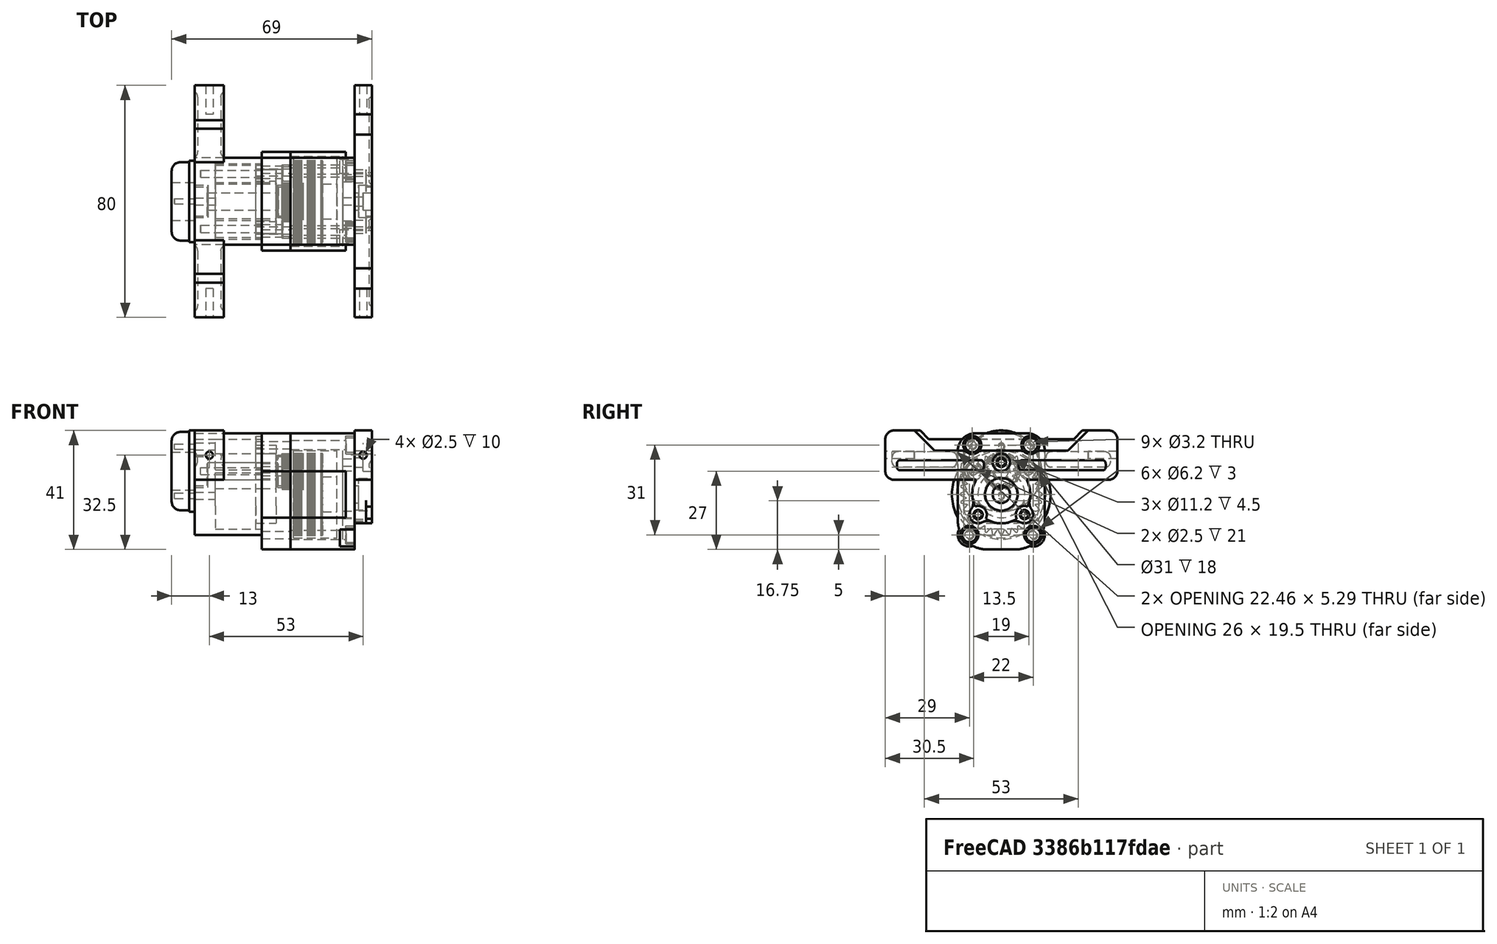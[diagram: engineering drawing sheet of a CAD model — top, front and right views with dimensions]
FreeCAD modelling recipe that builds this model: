
FCSTD DOCUMENT  (FreeCAD 0.14R3702 (Git))
Label: transfercase_box_02
License: CC-BY 3.0
LicenseURL: http://creativecommons.org/licenses/by/3.0/
objects: Part::Cylinder×106, Part::MultiFuse×53, Part::Cut×45, Part::Fillet×36, Part::Box×27, Part::Chamfer×3, Part::Feature×2
note: 272 computed .brp shape members not serialized (recipe doc carries the construction recipe); baked Part::Feature solids carry a one-line shape summary decoded from their .brp

FEATURE [Part::Box] Box
  Height = 40
  Length = 32
  Placement = pos=(23,0,0) rot=(0,0,1;0rad)
  Width = 30
FEATURE [Part::Box] Box001
  Height = 35
  Length = 23
  Placement = pos=(0,0,5) rot=(0,0,1;0rad)
  Width = 30
FEATURE [Part::Cylinder] Cylinder002
  Angle = 360
  Height = 6
  Placement = pos=(55,15,19) rot=(0,1,0;1.5708rad)
  Radius = 10
FEATURE [Part::Feature] difference002
  Placement = pos=(34,15,22) rot=(0,1,0;1.5708rad)
  shape: bbox 15 x 30 x 30 mm, 387 faces (baked)
FEATURE [Part::Cylinder] Cylinder003
  Angle = 360
  Height = 19
  Placement = pos=(33,15,19) rot=(0,1,0;1.5708rad)
  Radius = 17
FEATURE [Part::Feature] difference003
  Placement = pos=(29,16,29.5) rot=(0,1,0;1.5708rad)
  shape: bbox 15 x 12.44 x 12.35 mm, 184 faces (baked)
FEATURE [Part::Cylinder] Cylinder004
  Angle = 360
  Height = 4
  Placement = pos=(29,16,29.5) rot=(0,1,0;1.5708rad)
  Radius = 6.3
FEATURE [Part::Cut] Cut001
  Base = -> difference003
  Tool = -> Cylinder004
FEATURE [Part::Cylinder] Cylinder005
  Angle = 360
  Height = 1
  Placement = pos=(33,16,29.5) rot=(0,1,0;1.5708rad)
  Radius = 6.3
FEATURE [Part::MultiFuse] Fusion002
  Shapes = -> [Cylinder005,Cut001]
FEATURE [Part::Cylinder] Cylinder006
  Angle = 360
  Height = 5
  Placement = pos=(44,15,22) rot=(0,1,0;1.5708rad)
  Radius = 15
FEATURE [Part::MultiFuse] Fusion003
  Shapes = -> [difference002,Cylinder006]
FEATURE [Part::Cylinder] Cylinder007
  Angle = 360
  Height = 11
  Placement = pos=(33,16,29.5) rot=(0,1,0;1.5708rad)
  Radius = 2.5
FEATURE [Part::Box] Box002
  Height = 10
  Length = 10
  Placement = pos=(39,12,29.5) rot=(0,0,1;0rad)
  Width = 10
FEATURE [Part::Cut] Cut002
  Base = -> Cylinder007
  Tool = -> Box002
FEATURE [Part::Cut] Cut003  label="inner-gear_"
  Base = -> Fusion002
  Placement = pos=(-5,-1,-2.5) rot=(0,0,1;0rad)
  Tool = -> Cut002
FEATURE [Part::Cylinder] Cylinder009
  Angle = 360
  Height = 5
  Placement = pos=(44,15,22) rot=(0,1,0;1.5708rad)
  Radius = 6
FEATURE [Part::Cut] Cut004  label="outer-gear"
  Base = -> Fusion003
  Placement = pos=(0,0,-3) rot=(0,0,1;0rad)
  Tool = -> Cylinder009
FEATURE [Part::Fillet] Fillet002
  Base = -> Box001
  Edges = 2 edges r=10: [Edge9,Edge11]
FEATURE [Part::Fillet] Fillet003
  Base = -> Box
  Edges = 2 edges r=10: [Edge9,Edge11]
FEATURE [Part::Fillet] Fillet004
  Base = -> Fillet002
  Edges = 2 edges r=6: [Edge9,Edge12]
FEATURE [Part::Fillet] Fillet005
  Base = -> Fillet003
  Edges = 2 edges r=6: [Edge9,Edge12]
FEATURE [Part::MultiFuse] Fusion004
  Shapes = -> [Fillet005,Fillet004]
FEATURE [Part::Cylinder] Cylinder011
  Angle = 360
  Height = 2
  Placement = pos=(-2,15,27) rot=(0,1,0;1.5708rad)
  Radius = 14
FEATURE [Part::MultiFuse] Fusion006
  Shapes = -> [Fusion004,Cylinder003]
FEATURE [Part::Box] Box003  label="Cube"
  Height = 17
  Length = 10
  Placement = pos=(0,-25,24) rot=(0,0,1;0rad)
  Width = 80
FEATURE [Part::Fillet] Fillet006
  Base = -> Box003
  Edges = 4 edges r=3: [Edge9,Edge10,Edge11,Edge12]
FEATURE [Part::Box] Box004  label="Cube001"
  Height = 3
  Length = 10
  Placement = pos=(0,-10,38) rot=(0,0,1;0rad)
  Width = 50
FEATURE [Part::Cut] Cut
  Base = -> Fillet006
  Tool = -> Box004
FEATURE [Part::Chamfer] Chamfer
  Base = -> Cut
  Edges = 2 edges r=2.99: [Edge18,Edge25]
FEATURE [Part::Box] Box005
  Height = 35
  Length = 23
  Placement = pos=(0,0,5) rot=(0,0,1;0rad)
  Width = 30
FEATURE [Part::Cylinder] Cylinder
  Angle = 360
  Height = 17
  Placement = pos=(33,15,18) rot=(0,1,0;1.5708rad)
  Radius = 17
FEATURE [Part::Box] Box006
  Height = 40
  Length = 32
  Placement = pos=(23,0,0) rot=(0,0,1;0rad)
  Width = 30
FEATURE [Part::Fillet] Fillet
  Base = -> Box006
  Edges = 2 edges r=10: [Edge9,Edge11]
FEATURE [Part::Fillet] Fillet007
  Base = -> Fillet
  Edges = 2 edges r=6: [Edge9,Edge12]
FEATURE [Part::Fillet] Fillet008
  Base = -> Box005
  Edges = 2 edges r=10: [Edge9,Edge11]
FEATURE [Part::Fillet] Fillet009
  Base = -> Fillet008
  Edges = 2 edges r=6: [Edge9,Edge12]
FEATURE [Part::MultiFuse] Fusion007
  Shapes = -> [Fillet007,Fillet009]
FEATURE [Part::MultiFuse] Fusion
  Shapes = -> [Fusion007,Cylinder]
FEATURE [Part::Box] Box007
  Height = 40
  Length = 33
  Width = 30
FEATURE [Part::Box] Box008
  Height = 40
  Length = 22
  Placement = pos=(33,-3,0) rot=(0,0,1;0rad)
  Width = 36
FEATURE [Part::Cut] Cut005
  Base = -> Fusion006
  Tool = -> Box007
FEATURE [Part::Cut] Cut006
  Base = -> Fusion
  Tool = -> Box008
FEATURE [Part::Cylinder] Cylinder012
  Angle = 360
  Height = 18
  Placement = pos=(33,15,19) rot=(0,1,0;1.5708rad)
  Radius = 15.5
FEATURE [Part::Cylinder] Cylinder013
  Angle = 360
  Height = 25
  Placement = pos=(30,0,19) rot=(0,1,0;1.5708rad)
  Radius = 1.6
FEATURE [Part::Cylinder] Cylinder014
  Angle = 360
  Height = 4
  Placement = pos=(51,0,19) rot=(0,1,0;1.5708rad)
  Radius = 3.1
FEATURE [Part::MultiFuse] Fusion008
  Placement = pos=(0,4,-14) rot=(0,0,1;0rad)
  Shapes = -> [Cylinder014,Cylinder013]
FEATURE [Part::Cylinder] Cylinder015
  Angle = 360
  Height = 25
  Placement = pos=(30,0,19) rot=(0,1,0;1.5708rad)
  Radius = 1.6
FEATURE [Part::Cylinder] Cylinder016
  Angle = 360
  Height = 4
  Placement = pos=(51,0,19) rot=(0,1,0;1.5708rad)
  Radius = 3.1
FEATURE [Part::MultiFuse] Fusion009
  Placement = pos=(0,5,17) rot=(0,0,1;0rad)
  Shapes = -> [Cylinder016,Cylinder015]
FEATURE [Part::Cylinder] Cylinder017
  Angle = 360
  Height = 25
  Placement = pos=(30,0,19) rot=(0,1,0;1.5708rad)
  Radius = 1.6
FEATURE [Part::Cylinder] Cylinder018
  Angle = 360
  Height = 4
  Placement = pos=(51,0,19) rot=(0,1,0;1.5708rad)
  Radius = 3.1
FEATURE [Part::MultiFuse] Fusion010
  Placement = pos=(0,25,17) rot=(0,0,1;0rad)
  Shapes = -> [Cylinder018,Cylinder017]
FEATURE [Part::Cylinder] Cylinder019
  Angle = 360
  Height = 25
  Placement = pos=(30,0,19) rot=(0,1,0;1.5708rad)
  Radius = 1.6
FEATURE [Part::Cylinder] Cylinder020
  Angle = 360
  Height = 4
  Placement = pos=(51,0,19) rot=(0,1,0;1.5708rad)
  Radius = 3.1
FEATURE [Part::MultiFuse] Fusion011
  Placement = pos=(0,26,-14) rot=(0,0,1;0rad)
  Shapes = -> [Cylinder020,Cylinder019]
FEATURE [Part::Cylinder] Cylinder021
  Angle = 360
  Height = 5
  Placement = pos=(50,4,5) rot=(0,1,0;1.5708rad)
  Radius = 4
FEATURE [Part::Cylinder] Cylinder022
  Angle = 360
  Height = 5
  Placement = pos=(50,26,5) rot=(0,1,0;1.5708rad)
  Radius = 4
FEATURE [Part::MultiFuse] Fusion013
  Placement = pos=(1,0,0) rot=(0,0,1;0rad)
  Shapes = -> [Fusion008,Fusion010,Fusion011,Fusion009]
FEATURE [Part::MultiFuse] Fusion014
  Shapes = -> [Cut005,Cylinder022,Cylinder021]
FEATURE [Part::Cut] Cut007
  Base = -> Fusion014
  Tool = -> Cylinder012
FEATURE [Part::Cut] Cut008
  Base = -> Cut007
  Tool = -> Fusion013
FEATURE [Part::Cylinder] Cylinder023
  Angle = 360
  Height = 10
  Placement = pos=(23,15,19) rot=(0,1,0;1.5708rad)
  Radius = 17
FEATURE [Part::MultiFuse] Fusion015
  Shapes = -> [Cut006,Cylinder023]
FEATURE [Part::Cylinder] Cylinder024
  Angle = 360
  Height = 15
  Placement = pos=(30,5,36) rot=(0,1,0;1.5708rad)
  Radius = 1.25
FEATURE [Part::Cylinder] Cylinder025
  Angle = 360
  Height = 15
  Placement = pos=(30,25,36) rot=(0,1,0;1.5708rad)
  Radius = 1.25
FEATURE [Part::Cylinder] Cylinder026
  Angle = 360
  Height = 15
  Placement = pos=(30,26,5) rot=(0,1,0;1.5708rad)
  Radius = 1.25
FEATURE [Part::Cylinder] Cylinder027
  Angle = 360
  Height = 15
  Placement = pos=(30,4,5) rot=(0,1,0;1.5708rad)
  Radius = 1.25
FEATURE [Part::MultiFuse] Fusion016
  Placement = pos=(-12,0,0) rot=(0,0,1;0rad)
  Shapes = -> [Cylinder024,Cylinder027,Cylinder026,Cylinder025]
FEATURE [Part::Cut] Cut009
  Base = -> Fusion015
  Tool = -> Fusion016
FEATURE [Part::Cylinder] Cylinder029
  Angle = 360
  Height = 4.5
  Placement = pos=(28.5,15,27) rot=(0,1,0;1.5708rad)
  Radius = 5.6
FEATURE [Part::Cylinder] Cylinder030
  Angle = 360
  Height = 4.5
  Placement = pos=(0,15,27) rot=(0,1,0;1.5708rad)
  Radius = 5.6
FEATURE [Part::MultiFuse] Fusion017
  Shapes = -> [Chamfer,Cut009]
FEATURE [Part::Cylinder] Cylinder031
  Angle = 360
  Height = 33
  Placement = pos=(0,15,27) rot=(0,1,0;1.5708rad)
  Radius = 3
FEATURE [Part::MultiFuse] Fusion018
  Shapes = -> [Cylinder031,Cylinder030,Cylinder029]
FEATURE [Part::Cut] Cut010
  Base = -> Fusion017
  Tool = -> Fusion018
FEATURE [Part::Cylinder] Cylinder032
  Angle = 360
  Height = 5
  Placement = pos=(51,15,19) rot=(0,1,0;1.5708rad)
  Radius = 8.1
FEATURE [Part::Cut] Cut011
  Base = -> Cut008
  Tool = -> Cylinder032
FEATURE [Part::Cylinder] Cylinder033
  Angle = 360
  Height = 4
  Placement = pos=(57,15,19) rot=(0,1,0;1.5708rad)
  Radius = 5.6
FEATURE [Part::Cylinder] Cylinder034
  Angle = 360
  Height = 5
  Placement = pos=(55,15,19) rot=(0,1,0;1.5708rad)
  Radius = 3
FEATURE [Part::MultiFuse] Fusion019
  Shapes = -> [Cylinder033,Cylinder034]
FEATURE [Part::Cut] Cut012
  Base = -> Cylinder002
  Tool = -> Fusion019
FEATURE [Part::Cylinder] Cylinder035
  Angle = 360
  Height = 6
  Placement = pos=(55,23,12) rot=(0,1,0;1.5708rad)
  Radius = 3
FEATURE [Part::Box] Box009  label="Cube002"
  Height = 10
  Length = 6
  Placement = pos=(55,-25,24) rot=(0,0,1;0rad)
  Width = 80
FEATURE [Part::Cylinder] Cylinder036
  Angle = 360
  Height = 23
  Placement = pos=(-3,0,31) rot=(1,0,0;1.5708rad)
  Radius = 4
FEATURE [Part::Fillet] Fillet010
  Base = -> Cylinder036
  Edges = 2 edges r=2: [Edge1,Edge3]
FEATURE [Part::Cylinder] Cylinder037
  Angle = 360
  Height = 23
  Placement = pos=(-3,0,31) rot=(1,0,0;1.5708rad)
  Radius = 4
FEATURE [Part::Fillet] Fillet011
  Base = -> Cylinder037
  Edges = 2 edges r=2: [Edge1,Edge3]
  Placement = pos=(0,53,0) rot=(0,0,1;0rad)
FEATURE [Part::Cylinder] Cylinder038
  Angle = 360
  Height = 23
  Placement = pos=(-3,0,31) rot=(1,0,0;1.5708rad)
  Radius = 4
FEATURE [Part::Cylinder] Cylinder039
  Angle = 360
  Height = 23
  Placement = pos=(-3,0,31) rot=(1,0,0;1.5708rad)
  Radius = 4
FEATURE [Part::Fillet] Fillet012
  Base = -> Cylinder039
  Edges = 2 edges r=2: [Edge1,Edge3]
  Placement = pos=(16,0,0) rot=(0,0,1;0rad)
FEATURE [Part::Fillet] Fillet013
  Base = -> Cylinder038
  Edges = 2 edges r=2: [Edge1,Edge3]
  Placement = pos=(16,53,0) rot=(0,0,1;0rad)
FEATURE [Part::MultiFuse] Fusion020
  Shapes = -> [Fillet010,Fillet012,Fillet011,Fillet013]
FEATURE [Part::Cut] Cut013
  Base = -> Cut010
  Tool = -> Fusion020
FEATURE [Part::Cylinder] Cylinder040
  Angle = 360
  Height = 6
  Placement = pos=(55,7,12) rot=(0,1,0;1.5708rad)
  Radius = 3
FEATURE [Part::MultiFuse] Fusion021
  Shapes = -> [Cut012,Cylinder035,Cylinder040]
FEATURE [Part::Cylinder] Cylinder041
  Angle = 360
  Height = 3
  Placement = pos=(58,23,12) rot=(0,1,0;1.5708rad)
  Radius = 3
FEATURE [Part::Cylinder] Cylinder042
  Angle = 360
  Height = 3
  Placement = pos=(58,7,12) rot=(0,1,0;1.5708rad)
  Radius = 3
FEATURE [Part::Cylinder] Cylinder043
  Angle = 360
  Height = 10
  Placement = pos=(51,7,12) rot=(0,1,0;1.5708rad)
  Radius = 1.6
FEATURE [Part::Cylinder] Cylinder044
  Angle = 360
  Height = 10
  Placement = pos=(51,23,12) rot=(0,1,0;1.5708rad)
  Radius = 1.6
FEATURE [Part::MultiFuse] Fusion022
  Placement = pos=(1,0,0) rot=(0,0,1;0rad)
  Shapes = -> [Cylinder041,Cylinder042,Cylinder043,Cylinder044]
FEATURE [Part::Cut] Cut014
  Base = -> Fusion021
  Tool = -> Fusion022
FEATURE [Part::Cylinder] Cylinder045
  Angle = 360
  Height = 10
  Placement = pos=(47,7,12) rot=(0,1,0;1.5708rad)
  Radius = 1.25
FEATURE [Part::Cylinder] Cylinder046
  Angle = 360
  Height = 10
  Placement = pos=(46,23,12) rot=(0,1,0;1.5708rad)
  Radius = 1.25
FEATURE [Part::MultiFuse] Fusion023
  Shapes = -> [Cylinder046,Cylinder045]
FEATURE [Part::Cut] Cut015
  Base = -> Cut011
  Tool = -> Fusion023
FEATURE [Part::Box] Box010  label="Cube003"
  Height = 17
  Length = 6
  Placement = pos=(55,-25,24) rot=(0,0,1;0rad)
  Width = 10
FEATURE [Part::Box] Box011  label="Cube004"
  Height = 17
  Length = 6
  Placement = pos=(55,45,24) rot=(0,0,1;0rad)
  Width = 10
FEATURE [Part::Cylinder] Cylinder047
  Angle = 360
  Height = 3
  Placement = pos=(58,22,12) rot=(0,1,0;1.5708rad)
  Radius = 3
FEATURE [Part::Cylinder] Cylinder048
  Angle = 360
  Height = 10
  Placement = pos=(48,22,12) rot=(0,1,0;1.5708rad)
  Radius = 1.6
FEATURE [Part::MultiFuse] Fusion024
  Placement = pos=(0,-7,18) rot=(0,0,1;0rad)
  Shapes = -> [Cylinder048,Cylinder047]
FEATURE [Part::Cylinder] Cylinder049
  Angle = 360
  Height = 6
  Placement = pos=(55,15,19) rot=(0,1,0;1.5708rad)
  Radius = 5.6
FEATURE [Part::Cut] Cut016
  Base = -> Box009
  Tool = -> Cylinder049
FEATURE [Part::MultiFuse] Fusion025
  Shapes = -> [Box010,Box011,Cut016,Cut014]
FEATURE [Part::Cut] Cut017
  Base = -> Fusion025
  Tool = -> Fusion024
FEATURE [Part::Cylinder] Cylinder050
  Angle = 360
  Height = 10
  Placement = pos=(48,15,30) rot=(0,1,0;1.5708rad)
  Radius = 1.25
FEATURE [Part::Cut] Cut018  label="rear-part"
  Base = -> Cut015
  Tool = -> Cylinder050
FEATURE [Part::Fillet] Fillet014
  Base = -> Cut017
  Edges = 4 edges r=3: [Edge4,Edge44,Edge50,Edge53]
FEATURE [Part::Chamfer] Chamfer001
  Base = -> Fillet014
  Edges = 2 edges r=6.99: [Edge32,Edge54]
FEATURE [Part::Cylinder] Cylinder051
  Angle = 360
  Height = 10
  Placement = pos=(5,55,32.5) rot=(1,0,0;1.5708rad)
  Radius = 1.25
FEATURE [Part::Cylinder] Cylinder052
  Angle = 360
  Height = 10
  Placement = pos=(58,-15,32.5) rot=(1,0,0;1.5708rad)
  Radius = 1.25
FEATURE [Part::Cylinder] Cylinder053
  Angle = 360
  Height = 10
  Placement = pos=(5,-15,32.5) rot=(1,0,0;1.5708rad)
  Radius = 1.25
FEATURE [Part::Cylinder] Cylinder054
  Angle = 360
  Height = 10
  Placement = pos=(58,55,32.5) rot=(1,0,0;1.5708rad)
  Radius = 1.25
FEATURE [Part::MultiFuse] Fusion026
  Shapes = -> [Cylinder053,Cylinder051]
FEATURE [Part::MultiFuse] Fusion027
  Shapes = -> [Cylinder054,Cylinder052]
FEATURE [Part::Cut] Cut019
  Base = -> Cut013
  Tool = -> Fusion026
FEATURE [Part::Cylinder] Cylinder055
  Angle = 360
  Height = 10
  Placement = pos=(-10,15,27) rot=(0,1,0;1.5708rad)
  Radius = 6.5
FEATURE [Part::Cylinder] Cylinder056
  Angle = 360
  Height = 30
  Placement = pos=(62,9,29) rot=(1,0,0;1.5708rad)
  Radius = 2
FEATURE [Part::Fillet] Fillet016
  Base = -> Cylinder056
  Edges = 2 edges r=1: [Edge1,Edge3]
FEATURE [Part::Cylinder] Cylinder057
  Angle = 360
  Height = 30
  Placement = pos=(62,9,29) rot=(1,0,0;1.5708rad)
  Radius = 2
FEATURE [Part::Fillet] Fillet017
  Base = -> Cylinder057
  Edges = 2 edges r=1: [Edge1,Edge3]
  Placement = pos=(0,42,0) rot=(0,0,1;0rad)
FEATURE [Part::MultiFuse] Fusion028
  Shapes = -> [Fillet016,Fillet017]
FEATURE [Part::Cylinder] Cylinder058
  Angle = 360
  Height = 6
  Placement = pos=(-8,15,27) rot=(0,1,0;1.5708rad)
  Radius = 13.5
FEATURE [Part::MultiFuse] Fusion029
  Shapes = -> [Cylinder011,Cylinder058]
FEATURE [Part::Box] Box012  label="Cube005"
  Height = 17
  Length = 10
  Placement = pos=(0,-25,24) rot=(0,0,1;0rad)
  Width = 80
FEATURE [Part::Fillet] Fillet018
  Base = -> Box012
  Edges = 4 edges r=3: [Edge9,Edge10,Edge11,Edge12]
FEATURE [Part::Box] Box013  label="Cube006"
  Height = 3
  Length = 10
  Placement = pos=(0,-10,38) rot=(0,0,1;0rad)
  Width = 50
FEATURE [Part::Cut] Cut027
  Base = -> Fillet018
  Tool = -> Box013
FEATURE [Part::Chamfer] Chamfer002
  Base = -> Cut027
  Edges = 2 edges r=2.99: [Edge18,Edge25]
FEATURE [Part::Box] Box014
  Height = 40
  Length = 32
  Placement = pos=(23,0,0) rot=(0,0,1;0rad)
  Width = 30
FEATURE [Part::Fillet] Fillet020
  Base = -> Box014
  Edges = 2 edges r=10: [Edge9,Edge11]
FEATURE [Part::Fillet] Fillet019
  Base = -> Fillet020
  Edges = 2 edges r=6: [Edge9,Edge12]
FEATURE [Part::Box] Box015
  Height = 35
  Length = 23
  Placement = pos=(0,0,5) rot=(0,0,1;0rad)
  Width = 30
FEATURE [Part::Fillet] Fillet022
  Base = -> Box015
  Edges = 2 edges r=10: [Edge9,Edge11]
FEATURE [Part::Fillet] Fillet021
  Base = -> Fillet022
  Edges = 2 edges r=6: [Edge9,Edge12]
FEATURE [Part::MultiFuse] Fusion034
  Shapes = -> [Fillet019,Fillet021]
FEATURE [Part::Cylinder] Cylinder060
  Angle = 360
  Height = 17
  Placement = pos=(33,15,18) rot=(0,1,0;1.5708rad)
  Radius = 17
FEATURE [Part::MultiFuse] Fusion033
  Shapes = -> [Fusion034,Cylinder060]
FEATURE [Part::Box] Box016
  Height = 40
  Length = 22
  Placement = pos=(33,-3,0) rot=(0,0,1;0rad)
  Width = 36
FEATURE [Part::Cut] Cut029
  Base = -> Fusion033
  Tool = -> Box016
FEATURE [Part::Cylinder] Cylinder061
  Angle = 360
  Height = 10
  Placement = pos=(23,15,19) rot=(0,1,0;1.5708rad)
  Radius = 17
FEATURE [Part::MultiFuse] Fusion032
  Shapes = -> [Cut029,Cylinder061]
FEATURE [Part::Cylinder] Cylinder062
  Angle = 360
  Height = 15
  Placement = pos=(30,5,36) rot=(0,1,0;1.5708rad)
  Radius = 1.25
FEATURE [Part::Cylinder] Cylinder063
  Angle = 360
  Height = 15
  Placement = pos=(30,4,5) rot=(0,1,0;1.5708rad)
  Radius = 1.25
FEATURE [Part::Cylinder] Cylinder064
  Angle = 360
  Height = 15
  Placement = pos=(30,26,5) rot=(0,1,0;1.5708rad)
  Radius = 1.25
FEATURE [Part::Cylinder] Cylinder065
  Angle = 360
  Height = 15
  Placement = pos=(30,25,36) rot=(0,1,0;1.5708rad)
  Radius = 1.25
FEATURE [Part::MultiFuse] Fusion035
  Placement = pos=(-12,0,0) rot=(0,0,1;0rad)
  Shapes = -> [Cylinder062,Cylinder063,Cylinder064,Cylinder065]
FEATURE [Part::Cut] Cut028
  Base = -> Fusion032
  Tool = -> Fusion035
FEATURE [Part::MultiFuse] Fusion031
  Shapes = -> [Chamfer002,Cut028]
FEATURE [Part::Cylinder] Cylinder066
  Angle = 360
  Height = 33
  Placement = pos=(0,15,27) rot=(0,1,0;1.5708rad)
  Radius = 3
FEATURE [Part::Cylinder] Cylinder067
  Angle = 360
  Height = 4.5
  Placement = pos=(0,15,27) rot=(0,1,0;1.5708rad)
  Radius = 5.6
FEATURE [Part::Cylinder] Cylinder068
  Angle = 360
  Height = 4.5
  Placement = pos=(28.5,15,27) rot=(0,1,0;1.5708rad)
  Radius = 5.6
FEATURE [Part::MultiFuse] Fusion036
  Shapes = -> [Cylinder066,Cylinder067,Cylinder068]
FEATURE [Part::Cut] Cut026
  Base = -> Fusion031
  Tool = -> Fusion036
FEATURE [Part::Cylinder] Cylinder069
  Angle = 360
  Height = 23
  Placement = pos=(-3,0,31) rot=(1,0,0;1.5708rad)
  Radius = 4
FEATURE [Part::Fillet] Fillet023
  Base = -> Cylinder069
  Edges = 2 edges r=2: [Edge1,Edge3]
FEATURE [Part::Cylinder] Cylinder070
  Angle = 360
  Height = 23
  Placement = pos=(-3,0,31) rot=(1,0,0;1.5708rad)
  Radius = 4
FEATURE [Part::Fillet] Fillet024
  Base = -> Cylinder070
  Edges = 2 edges r=2: [Edge1,Edge3]
  Placement = pos=(16,0,0) rot=(0,0,1;0rad)
FEATURE [Part::Cylinder] Cylinder071
  Angle = 360
  Height = 23
  Placement = pos=(-3,0,31) rot=(1,0,0;1.5708rad)
  Radius = 4
FEATURE [Part::Fillet] Fillet025
  Base = -> Cylinder071
  Edges = 2 edges r=2: [Edge1,Edge3]
  Placement = pos=(0,53,0) rot=(0,0,1;0rad)
FEATURE [Part::Cylinder] Cylinder072
  Angle = 360
  Height = 23
  Placement = pos=(-3,0,31) rot=(1,0,0;1.5708rad)
  Radius = 4
FEATURE [Part::Fillet] Fillet026
  Base = -> Cylinder072
  Edges = 2 edges r=2: [Edge1,Edge3]
  Placement = pos=(16,53,0) rot=(0,0,1;0rad)
FEATURE [Part::MultiFuse] Fusion037
  Shapes = -> [Fillet023,Fillet024,Fillet025,Fillet026]
FEATURE [Part::Cut] Cut025
  Base = -> Cut026
  Tool = -> Fusion037
FEATURE [Part::Cylinder] Cylinder073
  Angle = 360
  Height = 10
  Placement = pos=(5,-15,32.5) rot=(1,0,0;1.5708rad)
  Radius = 1.25
FEATURE [Part::Cylinder] Cylinder074
  Angle = 360
  Height = 10
  Placement = pos=(5,55,32.5) rot=(1,0,0;1.5708rad)
  Radius = 1.25
FEATURE [Part::MultiFuse] Fusion038
  Shapes = -> [Cylinder073,Cylinder074]
FEATURE [Part::Cut] Cut024
  Base = -> Cut025
  Tool = -> Fusion038
FEATURE [Part::Box] Box017
  Height = 41
  Length = 23
  Placement = pos=(0,-25,0) rot=(0,0,1;0rad)
  Width = 80
FEATURE [Part::Box] Box018
  Height = 41
  Length = 23
  Placement = pos=(23,-25,0) rot=(0,0,1;0rad)
  Width = 80
FEATURE [Part::Cut] Cut031
  Base = -> Cut024
  Tool = -> Box017
FEATURE [Part::Box] Box019
  Height = 31
  Length = 18
  Placement = pos=(5,2,7) rot=(0,0,1;0rad)
  Width = 26
FEATURE [Part::Cut] Cut032
  Base = -> Cut019
  Tool = -> Box018
FEATURE [Part::Fillet] Fillet027
  Base = -> Box019
  Edges = 2 edges r=4: [Edge10,Edge12]
FEATURE [Part::Fillet] Fillet028
  Base = -> Fillet027
  Edges = 2 edges r=8: [Edge9,Edge12]
  Placement = pos=(2,0,0) rot=(0,0,1;0rad)
FEATURE [Part::Cut] Cut033
  Base = -> Cut032
  Tool = -> Fillet028
FEATURE [Part::Cylinder] Cylinder075
  Angle = 360
  Height = 16
  Placement = pos=(7,15,27) rot=(0,1,0;1.5708rad)
  Radius = 3
FEATURE [Part::Cylinder] Cylinder076
  Angle = 360
  Height = 16
  Placement = pos=(7,15,27) rot=(0,1,0;1.5708rad)
  Radius = 6
FEATURE [Part::Box] Box020  label="Cube007"
  Height = 1
  Length = 16
  Placement = pos=(7,2,26.5) rot=(0,0,1;0rad)
  Width = 26
FEATURE [Part::MultiFuse] Fusion039
  Shapes = -> [Cylinder076,Box020]
FEATURE [Part::Cut] Cut034
  Base = -> Fusion039
  Tool = -> Cylinder075
FEATURE [Part::MultiFuse] Fusion040
  Shapes = -> [Cut033,Cut034]
FEATURE [Part::Box] Box021
  Height = 31
  Length = 18
  Placement = pos=(5,2,7) rot=(0,0,1;0rad)
  Width = 26
FEATURE [Part::Fillet] Fillet030
  Base = -> Box021
  Edges = 2 edges r=4: [Edge10,Edge12]
FEATURE [Part::Fillet] Fillet029
  Base = -> Fillet030
  Edges = 2 edges r=8: [Edge9,Edge12]
  Placement = pos=(5,0,0) rot=(0,0,1;0rad)
FEATURE [Part::Cylinder] Cylinder077
  Angle = 360
  Height = 5
  Placement = pos=(23,15,27) rot=(0,1,0;1.5708rad)
  Radius = 6
FEATURE [Part::Cut] Cut035
  Base = -> Cut031
  Tool = -> Fillet029
FEATURE [Part::Cylinder] Cylinder078
  Angle = 360
  Height = 5
  Placement = pos=(23,15,27) rot=(0,1,0;1.5708rad)
  Radius = 3
FEATURE [Part::Box] Box022  label="Cube008"
  Height = 1
  Length = 5
  Placement = pos=(23,2,26.5) rot=(0,0,1;0rad)
  Width = 26
FEATURE [Part::MultiFuse] Fusion041
  Shapes = -> [Cylinder077,Box022]
FEATURE [Part::Cut] Cut036
  Base = -> Fusion041
  Tool = -> Cylinder078
FEATURE [Part::MultiFuse] Fusion042
  Shapes = -> [Cut035,Cut036]
FEATURE [Part::Box] Box023
  Height = 31
  Length = 7
  Placement = pos=(5,2,7) rot=(0,0,1;0rad)
  Width = 26
FEATURE [Part::Fillet] Fillet032
  Base = -> Box023
  Edges = 2 edges r=4: [Edge10,Edge12]
FEATURE [Part::Fillet] Fillet031
  Base = -> Fillet032
  Edges = 2 edges r=8: [Edge9,Edge12]
  Placement = pos=(5,0,0) rot=(0,0,1;0rad)
FEATURE [Part::Box] Box024
  Height = 27
  Length = 7
  Placement = pos=(10,4,9) rot=(0,0,1;0rad)
  Width = 22
FEATURE [Part::Fillet] Fillet033
  Base = -> Box024
  Edges = 2 edges r=6: [Edge9,Edge11]
  Placement = pos=(-2,0,0) rot=(0,0,1;0rad)
FEATURE [Part::Fillet] Fillet034
  Base = -> Fillet033
  Edges = 2 edges r=2: [Edge9,Edge12]
  Placement = pos=(2,0,0) rot=(0,0,1;0rad)
FEATURE [Part::Cut] Cut037
  Base = -> Fillet031
  Placement = pos=(11,0,0) rot=(0,0,1;0rad)
  Tool = -> Fillet034
FEATURE [Part::Box] Box025  label="Cube009"
  Height = 2
  Length = 2
  Placement = pos=(21,2,26) rot=(0,0,1;0rad)
  Width = 2
FEATURE [Part::Box] Box026  label="Cube010"
  Height = 2
  Length = 2
  Placement = pos=(21,26,26) rot=(0,0,1;0rad)
  Width = 2
FEATURE [Part::MultiFuse] Fusion043
  Shapes = -> [Box025,Box026]
FEATURE [Part::Cut] Cut038
  Base = -> Cut037
  Tool = -> Fusion043
FEATURE [Part::MultiFuse] Fusion044
  Shapes = -> [Fusion042,Cut038]
FEATURE [Part::Cylinder] Cylinder079
  Angle = 360
  Height = 12
  Placement = pos=(21,5,36) rot=(0,1,0;1.5708rad)
  Radius = 3
FEATURE [Part::Cylinder] Cylinder080
  Angle = 360
  Height = 12
  Placement = pos=(21,5,36) rot=(0,1,0;1.5708rad)
  Radius = 1.25
FEATURE [Part::Cylinder] Cylinder081
  Angle = 360
  Height = 12
  Placement = pos=(21,25,36) rot=(0,1,0;1.5708rad)
  Radius = 3
FEATURE [Part::Cylinder] Cylinder082
  Angle = 360
  Height = 12
  Placement = pos=(21,25,36) rot=(0,1,0;1.5708rad)
  Radius = 1.25
FEATURE [Part::MultiFuse] Fusion045
  Shapes = -> [Cylinder079,Cylinder081,Fusion044]
FEATURE [Part::MultiFuse] Fusion046
  Shapes = -> [Cylinder080,Cylinder082]
FEATURE [Part::Cut] Cut039
  Base = -> Fusion045
  Tool = -> Fusion046
FEATURE [Part::Cylinder] Cylinder083
  Angle = 360
  Height = 23
  Placement = pos=(0,5.5,27) rot=(0,1,0;1.5708rad)
  Radius = 3
FEATURE [Part::Cylinder] Cylinder084
  Angle = 360
  Height = 23
  Placement = pos=(0,24.5,27) rot=(0,1,0;1.5708rad)
  Radius = 3
FEATURE [Part::Cylinder] Cylinder085
  Angle = 360
  Height = 23
  Placement = pos=(0,24.5,27) rot=(0,1,0;1.5708rad)
  Radius = 1.25
FEATURE [Part::Cylinder] Cylinder086
  Angle = 360
  Height = 23
  Placement = pos=(0,5.5,27) rot=(0,1,0;1.5708rad)
  Radius = 1.25
FEATURE [Part::MultiFuse] Fusion047
  Shapes = -> [Cylinder084,Cylinder083,Fusion040]
FEATURE [Part::MultiFuse] Fusion048
  Placement = pos=(2,0,0) rot=(0,0,1;0rad)
  Shapes = -> [Cylinder085,Cylinder086]
FEATURE [Part::Cut] Cut040  label="front-part_"
  Base = -> Fusion047
  Tool = -> Fusion048
FEATURE [Part::Cylinder] Cylinder087
  Angle = 360
  Height = 2
  Placement = pos=(21,24.5,27) rot=(0,1,0;1.5708rad)
  Radius = 3.2
FEATURE [Part::Cylinder] Cylinder088
  Angle = 360
  Height = 2
  Placement = pos=(21,5.5,27) rot=(0,1,0;1.5708rad)
  Radius = 3.2
FEATURE [Part::Cylinder] Cylinder089
  Angle = 360
  Height = 10
  Placement = pos=(23,24.5,27) rot=(0,1,0;1.5708rad)
  Radius = 3
FEATURE [Part::Cylinder] Cylinder090
  Angle = 360
  Height = 10
  Placement = pos=(23,5.5,27) rot=(0,1,0;1.5708rad)
  Radius = 3
FEATURE [Part::MultiFuse] Fusion049
  Shapes = -> [Cylinder089,Cylinder090,Cut039]
FEATURE [Part::MultiFuse] Fusion050
  Shapes = -> [Cylinder088,Cylinder087]
FEATURE [Part::Cut] Cut041
  Base = -> Fusion049
  Tool = -> Fusion050
FEATURE [Part::Cylinder] Cylinder091
  Angle = 360
  Height = 10
  Placement = pos=(23,5.5,27) rot=(0,1,0;1.5708rad)
  Radius = 1.6
FEATURE [Part::Cylinder] Cylinder092
  Angle = 360
  Height = 10
  Placement = pos=(23,24.5,27) rot=(0,1,0;1.5708rad)
  Radius = 1.6
FEATURE [Part::Cylinder] Cylinder093
  Angle = 360
  Height = 3
  Placement = pos=(30,5.5,27) rot=(0,1,0;1.5708rad)
  Radius = 3.1
FEATURE [Part::Cylinder] Cylinder094
  Angle = 360
  Height = 3
  Placement = pos=(30,24.5,27) rot=(0,1,0;1.5708rad)
  Radius = 3.1
FEATURE [Part::MultiFuse] Fusion051
  Shapes = -> [Cylinder091,Cylinder092,Cylinder094,Cylinder093]
FEATURE [Part::Cut] Cut042  label="middle-part"
  Base = -> Cut041
  Tool = -> Fusion051
FEATURE [Part::Cylinder] Cylinder095
  Angle = 360
  Height = 2.7
  Placement = pos=(30.3,5.5,27) rot=(0,1,0;1.5708rad)
  Radius = 2.5
FEATURE [Part::Cylinder] Cylinder096
  Angle = 360
  Height = 2.7
  Placement = pos=(30.3,24.5,27) rot=(0,1,0;1.5708rad)
  Radius = 2.5
FEATURE [Part::Cylinder] Cylinder097
  Angle = 360
  Height = 4.2
  Placement = pos=(28.8,15,27) rot=(0,1,0;1.5708rad)
  Radius = 5
FEATURE [Part::MultiFuse] Fusion052  label="middle-part-support"
  Shapes = -> [Cylinder097,Cylinder095,Cylinder096]
FEATURE [Part::Cylinder] Cylinder098  label="front-part-support"
  Angle = 360
  Height = 4.2
  Placement = pos=(0,15,27) rot=(0,1,0;1.5708rad)
  Radius = 5
FEATURE [Part::Cut] Cut043
  Base = -> Chamfer001
  Tool = -> Fusion027
FEATURE [Part::Cut] Cut044  label="exit-part_"
  Base = -> Cut043
  Tool = -> Fusion028
FEATURE [Part::Fillet] Fillet035  label="exit-part__"
  Base = -> Cut044
  Edges = 4 edges r=4: [Edge56,Edge65,Edge71,Edge76]
FEATURE [Part::Cylinder] Cylinder099
  Angle = 360
  Height = 2.7
  Placement = pos=(52.3,5,36) rot=(0,1,0;1.5708rad)
  Radius = 2.5
FEATURE [Part::Cylinder] Cylinder100
  Angle = 360
  Height = 2.7
  Placement = pos=(52.3,25,36) rot=(0,1,0;1.5708rad)
  Radius = 2.5
FEATURE [Part::Cylinder] Cylinder101
  Angle = 360
  Height = 2.7
  Placement = pos=(52.3,26,5) rot=(0,1,0;1.5708rad)
  Radius = 2.5
FEATURE [Part::Cylinder] Cylinder102
  Angle = 360
  Height = 2.7
  Placement = pos=(52.3,4,5) rot=(0,1,0;1.5708rad)
  Radius = 2.5
FEATURE [Part::MultiFuse] Fusion053  label="rear-part-support"
  Shapes = -> [Cylinder099,Cylinder101,Cylinder100,Cylinder102]
FEATURE [Part::Cylinder] Cylinder103
  Angle = 360
  Height = 6
  Placement = pos=(55,5,36) rot=(0,1,0;1.5708rad)
  Radius = 3.1
FEATURE [Part::Cylinder] Cylinder104
  Angle = 360
  Height = 6
  Placement = pos=(55,25,36) rot=(0,1,0;1.5708rad)
  Radius = 3.1
FEATURE [Part::MultiFuse] Fusion054
  Shapes = -> [Cylinder104,Cylinder103]
FEATURE [Part::Cut] Cut045
  Base = -> Fillet035
  Tool = -> Fusion054
FEATURE [Part::Fillet] Fillet037  label="exit-part__001"
  Base = -> Cut045
  Edges = 4 edges r=2: [Edge58,Edge63,Edge64,Edge69]
FEATURE [Part::Cylinder] Cylinder105
  Angle = 360
  Height = 10
  Placement = pos=(0,15,35.5) rot=(0,1,0;1.5708rad)
  Radius = 1.2
FEATURE [Part::Cylinder] Cylinder106
  Angle = 360
  Height = 10
  Placement = pos=(0,15,18.5) rot=(0,1,0;1.5708rad)
  Radius = 1.2
FEATURE [Part::MultiFuse] Fusion055
  Shapes = -> [Cylinder106,Cylinder105]
FEATURE [Part::Cut] Cut046  label="front-part"
  Base = -> Cut040
  Tool = -> Fusion055
FEATURE [Part::Cylinder] Cylinder107
  Angle = 360
  Height = 7
  Placement = pos=(-7,15,18.5) rot=(0,1,0;1.5708rad)
  Radius = 0.9
FEATURE [Part::Cylinder] Cylinder108
  Angle = 360
  Height = 7
  Placement = pos=(-7,15,35.5) rot=(0,1,0;1.5708rad)
  Radius = 0.9
FEATURE [Part::MultiFuse] Fusion056
  Shapes = -> [Cylinder107,Cylinder055,Cylinder108]
FEATURE [Part::Cut] Cut047
  Base = -> Fusion029
  Tool = -> Fusion056
FEATURE [Part::Fillet] Fillet038  label="clutch-part"
  Base = -> Cut047
  Edges = 1 edges r=3: [Edge15]
FEATURE [Part::Cylinder] Cylinder109
  Angle = 360
  Height = 4.5
  Placement = pos=(56.5,15,19) rot=(0,1,0;1.5708rad)
  Radius = 5.6
FEATURE [Part::Cut] Cut048  label="exit-part"
  Base = -> Fillet037
  Tool = -> Cylinder109
FEATURE [Part::Cylinder] Cylinder110
  Angle = 360
  Height = 2
  Placement = pos=(28,15,27) rot=(0,1,0;1.5708rad)
  Radius = 6.3
FEATURE [Part::Cut] Cut049  label="inner-gear"
  Base = -> Cut003
  Tool = -> Cylinder110
